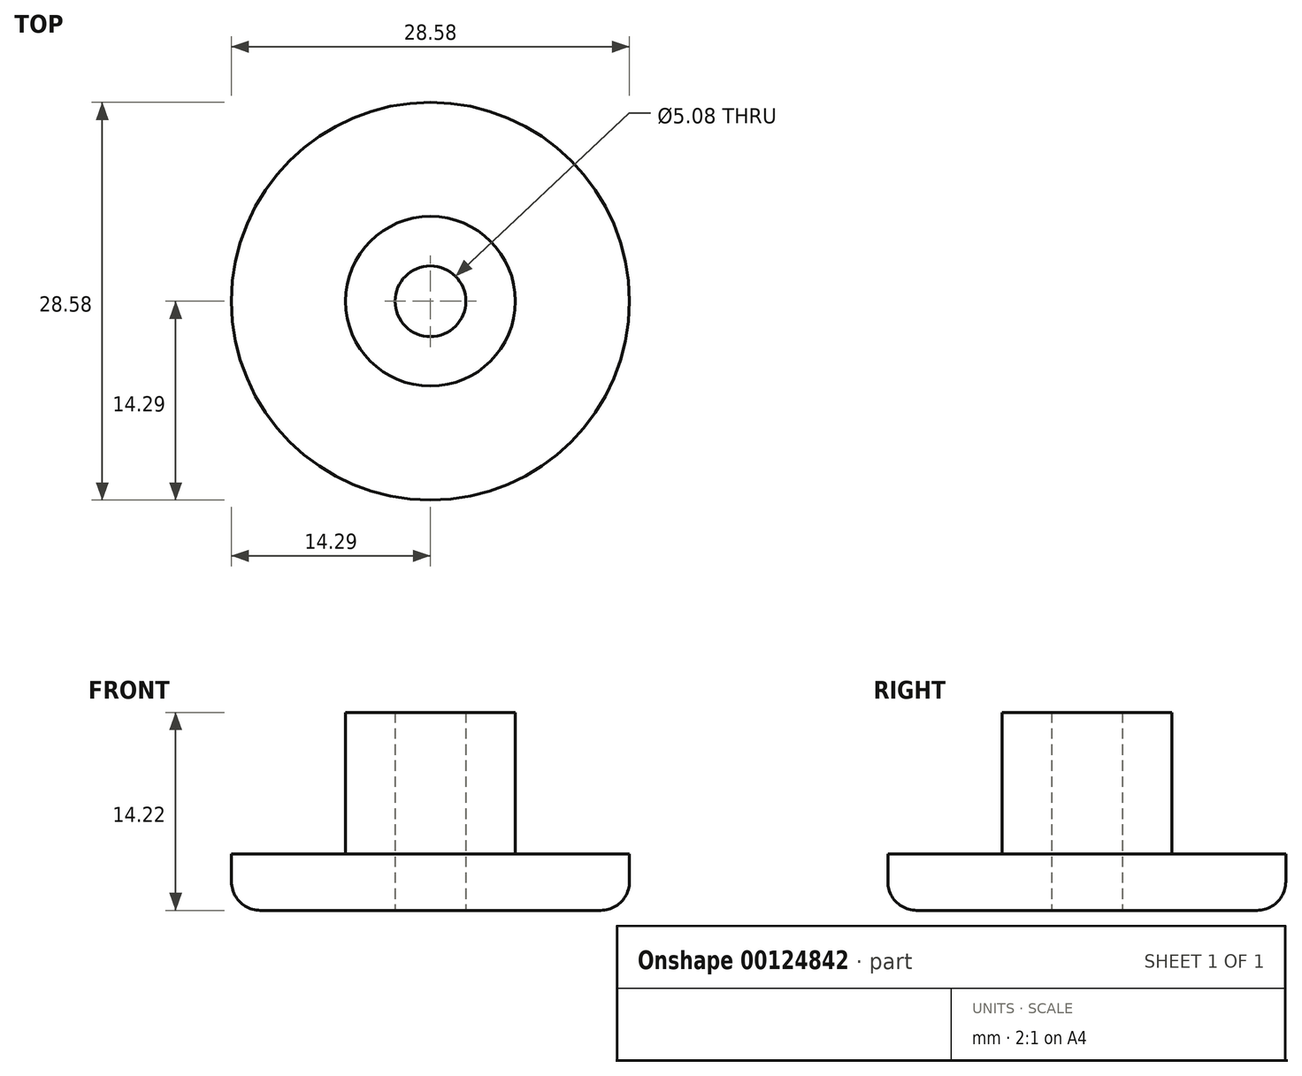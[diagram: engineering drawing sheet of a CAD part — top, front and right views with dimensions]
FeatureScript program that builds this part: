
annotation { "Feature Type Name" : "Feature", "Feature Type Description" : "" }
export const myFeature = defineFeature(function(context is Context, id is Id, definition is map)
    precondition{}
    {
        {
            var Q0;
            Q0=qCreatedBy(makeId("Top.planeOp"),FACE);
            var sketch = newSketch(context, id + "F0", { "sketchPlane" : qUnion([Q0])});
            skCircle(sketch, "E0", {"center": v(0, 0) * mm, "radius": 14.29 * mm});
            skCircle(sketch, "E1", {"center": v(0, 0) * mm, "radius": 6.1 * mm});
            skCircle(sketch, "E2", {"center": v(0, 0) * mm, "radius": 2.54 * mm});
            skSolve(sketch);
        }
        {
            var Q0;
            Q0=makeQuery(id+"F0.imprint","IMPRINT",FACE,{"disambiguationData":[TD([[makeQuery(id+"F0.imprint","IMPRINT",EDGE,{"derivedFrom":sQuery(id+"F0.wireOp",EDGE,"E0")}),1.0]])]});
            var Q1;
            Q1=makeQuery(id+"F0.imprint","IMPRINT",FACE,{"disambiguationData":[TD([[makeQuery(id+"F0.imprint","IMPRINT",EDGE,{"derivedFrom":sQuery(id+"F0.wireOp",EDGE,"E1")}),1.0]])]});
            extrude(context, id + "F1", {"entities" : qUnion([Q0, Q1]), "depth" : 4.06 * mm});
        }
        {
            var Q0;
            Q0=makeQuery(id+"F0.imprint","IMPRINT",FACE,{"disambiguationData":[TD([[makeQuery(id+"F0.imprint","IMPRINT",EDGE,{"derivedFrom":sQuery(id+"F0.wireOp",EDGE,"E1")}),1.0]])]});
            extrude(context, id + "F2", {"entities" : qUnion([Q0]), "operationType" : NewBodyOperationType.ADD, "depth" : 14.22 * mm});
        }
        {
            var Q0;
            Q0=makeQuery(id+"F1.opExtrude","CAP_EDGE",EDGE,{"disambiguationData":[OSD([sQuery(id+"F0.wireOp",EDGE,"E0")])],"isStart":true});
            fillet(context, id + "F3", {"entities" : qUnion([Q0]), "radius" : 2.06 * mm, "tangentPropagation" : true, "allowEdgeOverflow" : false});
        }
    });
